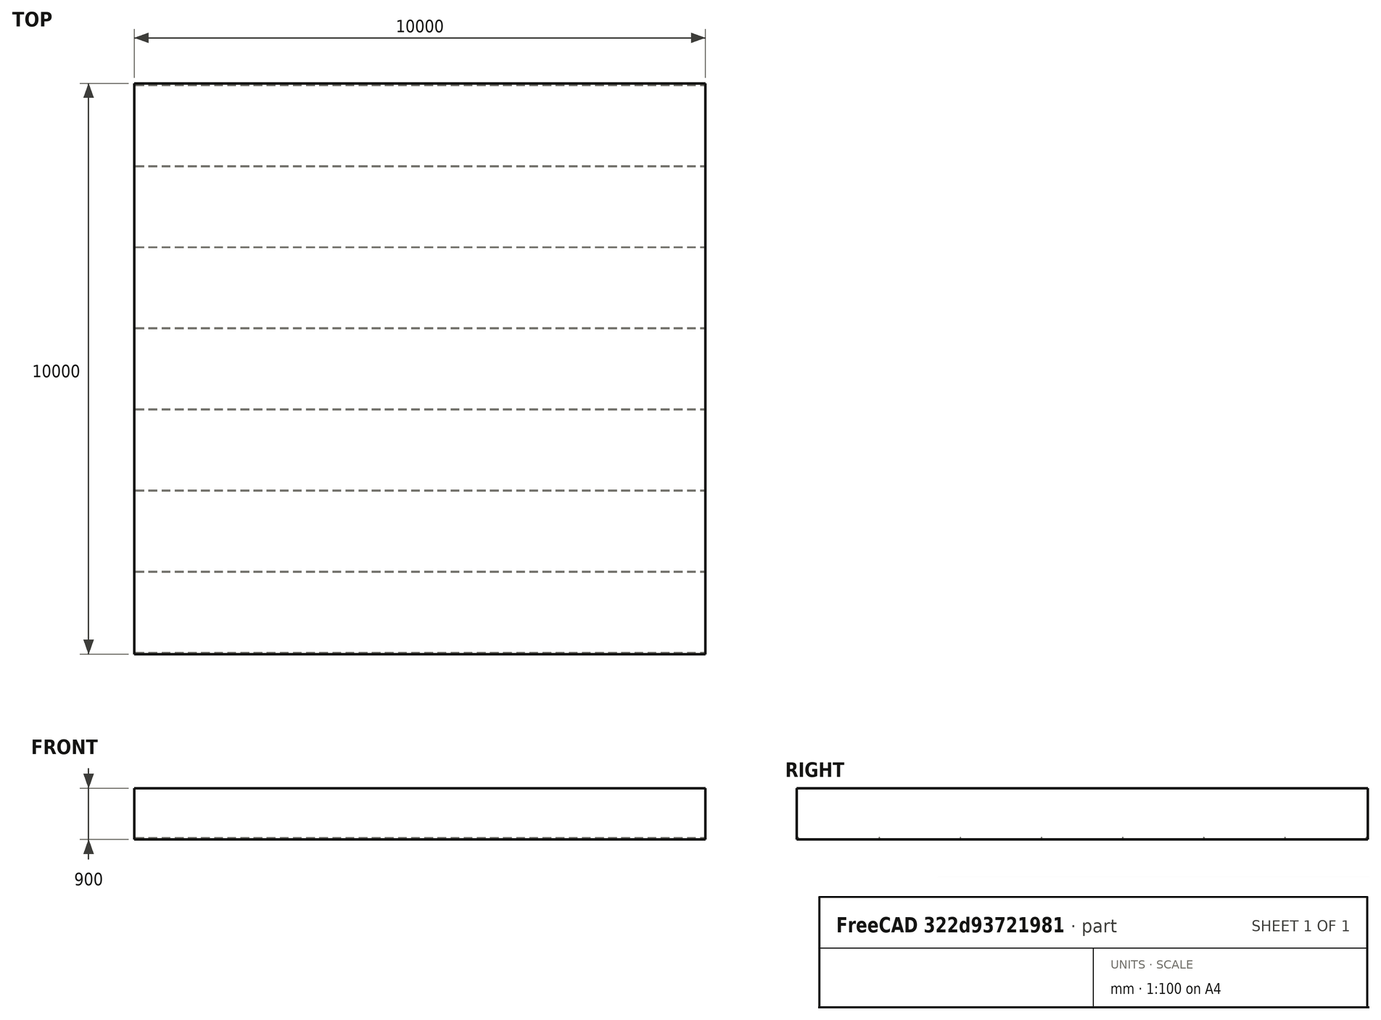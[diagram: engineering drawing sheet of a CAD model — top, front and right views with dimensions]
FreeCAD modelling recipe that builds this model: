
FCSTD DOCUMENT  (FreeCAD 0.19R24276 (Git))
Label: Slab with reinforcement
License: All rights reserved
LicenseURL: http://en.wikipedia.org/wiki/All_rights_reserved
objects: Part::FeaturePython×2, Part::Part2DObjectPython×1, Sketcher::SketchObject×1
note: 4 computed .brp shape members not serialized (recipe doc carries the construction recipe); baked Part::Feature solids carry a one-line shape summary decoded from their .brp

FEATURE [Part::Part2DObjectPython] Rectangle  # Draft 2D object (typed FeaturePython)
  Area = 100000000
  ChamferSize = 0
  Columns = 1
  FilletRadius = 0
  Height = 1000
  Length = 0
  MakeFace = true
  Placement = pos=(-10000,0,0) rot=(0,0,1;0rad)
  Rows = 1
FEATURE [Part::FeaturePython] Structure  # Arch/BIM 172 (typed FeaturePython)
  Base = -> Rectangle
  FaceMaker = 0
  Height = 900
  HorizontalArea = 100000000
  IfcData = attributes={"GlobalId": {"name": "GlobalId", "type": "IfcGloballyUniqueId", "is_enum": false, "enum_values": []}, "Description": {"... (+484 chars omitted),+1 more (map truncated)
  IfcType = 172
  Length = 0
  MoveBase = false
  MoveWithHost = false
  Nodes = (2) [(-5000,5000,0),(-5000,5000,900)]
  NodesOffset = 0
  Normal = (0,0,0)
  PerimeterLength = 40000
  PredefinedType = 0
  VerticalArea = 36000000
  Width = 180
FEATURE [Sketcher::SketchObject] Sketch
  FullyConstrained = false
  MapMode = 5
  Placement = pos=(0,0,0) rot=(1,0,0;1.5708rad)
  Support = -> [Structure]
  sketch-geometry (1):
    g0: LineSegment StartX=-9980 StartY=26 StartZ=0 EndX=-22 EndY=26 EndZ=0
FEATURE [Part::FeaturePython] Rebar  label="StraightRebar"  # Arch/BIM 110 (typed FeaturePython)
  Amount = 8
  AmountCheck = true
  Base = -> Sketch
  Cover = 20
  CoverAlong = Bottom Side
  Diameter = 12
  Direction = (0,0,0)
  Distance = 0
  FrontCover = 20
  HorizontalArea = 0
  Host = -> Structure
  IfcType = 110
  LeftBottomCover = 20
  Length = 9958
  Mark = StraightRebar
  MoveBase = false
  MoveWithHost = false
  OffsetEnd = 26
  OffsetStart = 26
  Orientation = Horizontal
  PerimeterLength = 0
  PlacementList = 8 placements: arithmetic series from (0,26,-5.77316e-15) step (0,1421.14,-3.15557e-13) to (0,9974,-2.21467e-12)
  RebarShape = 0
  RightTopCover = 22
  Rounding = 0
  Spacing = 1421.14
  TotalLength = 79664
  TrueSpacing = 8
  VerticalArea = 0
